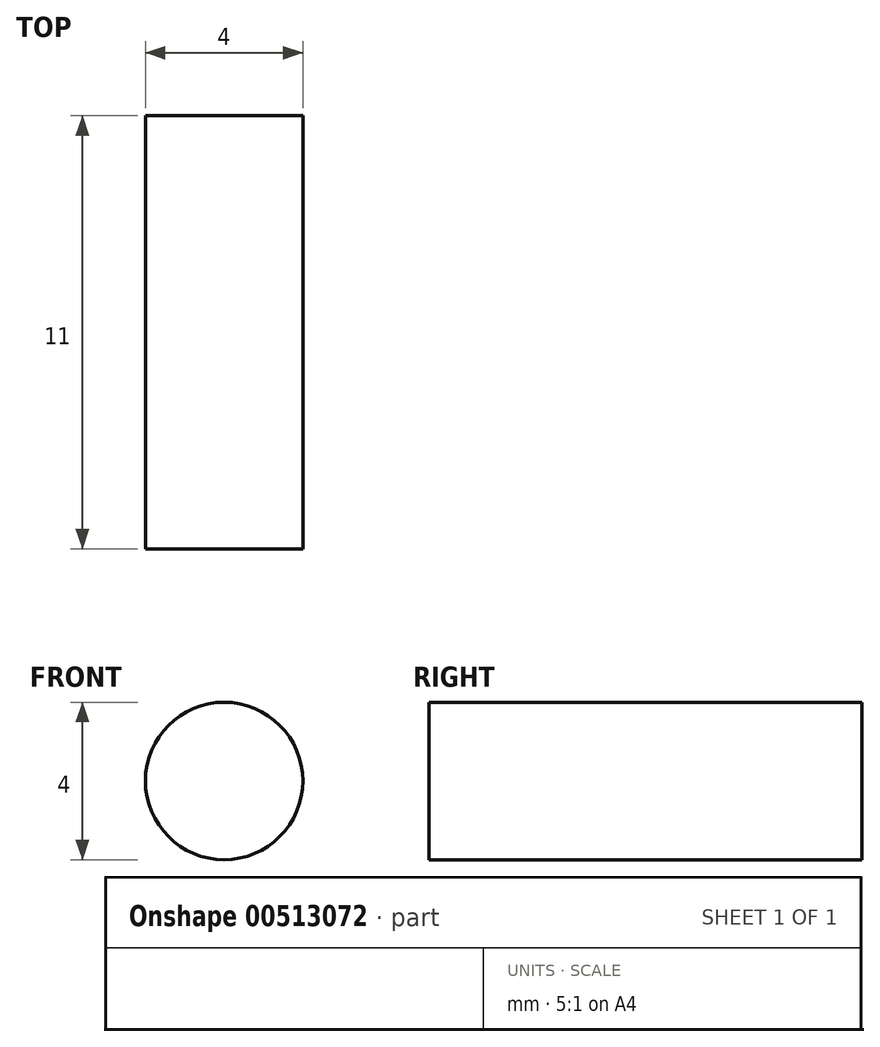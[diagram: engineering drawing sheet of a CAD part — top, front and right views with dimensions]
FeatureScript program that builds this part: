
annotation { "Feature Type Name" : "Feature", "Feature Type Description" : "" }
export const myFeature = defineFeature(function(context is Context, id is Id, definition is map)
    precondition{}
    {
        {
            var Q0;
            Q0=qCreatedBy(makeId("Front.planeOp"),FACE);
            var sketch = newSketch(context, id + "F0", { "sketchPlane" : qUnion([Q0])});
            skCircle(sketch, "E0", {"center": v(0, 0) * mm, "radius": 2 * mm});
            skSolve(sketch);
        }
        {
            var Q0;
            Q0 = qSketchRegion(id + "F0", true);
            extrude(context, id + "F1", {"entities" : qUnion([Q0]), "depth" : 11 * mm});
        }
    });
